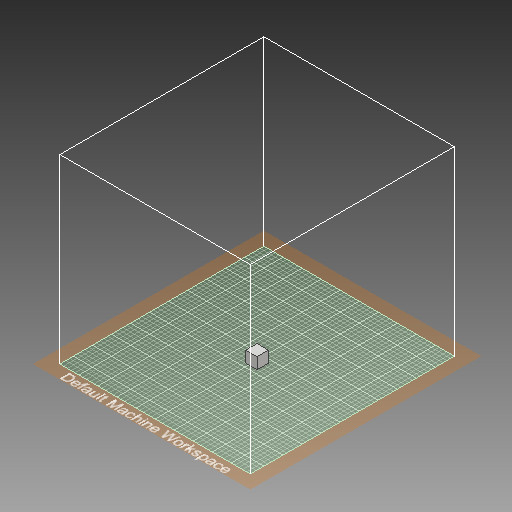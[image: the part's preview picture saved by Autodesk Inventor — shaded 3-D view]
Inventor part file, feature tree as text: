
AUTODESK INVENTOR PART (.ipt)
format: ipt  version: 2019 (Build 230136000, 136)  size: 216,576 bytes
history: native  units: mm
features: extrude x1, sketch x1
ambient origin geometry x8: Origin, YZ Plane, XZ Plane, XY Plane, X Axis, Y Axis, Z Axis, Center Point
bodies: Solid1 (feature_tree)
feature tree (2):
  extrude  "Extrusion1"  Depth=35.0mm
  sketch  "Sketch1"  dims[d0=35.0mm d1=35.0mm d2=35.0mm d3=0.0mm]
